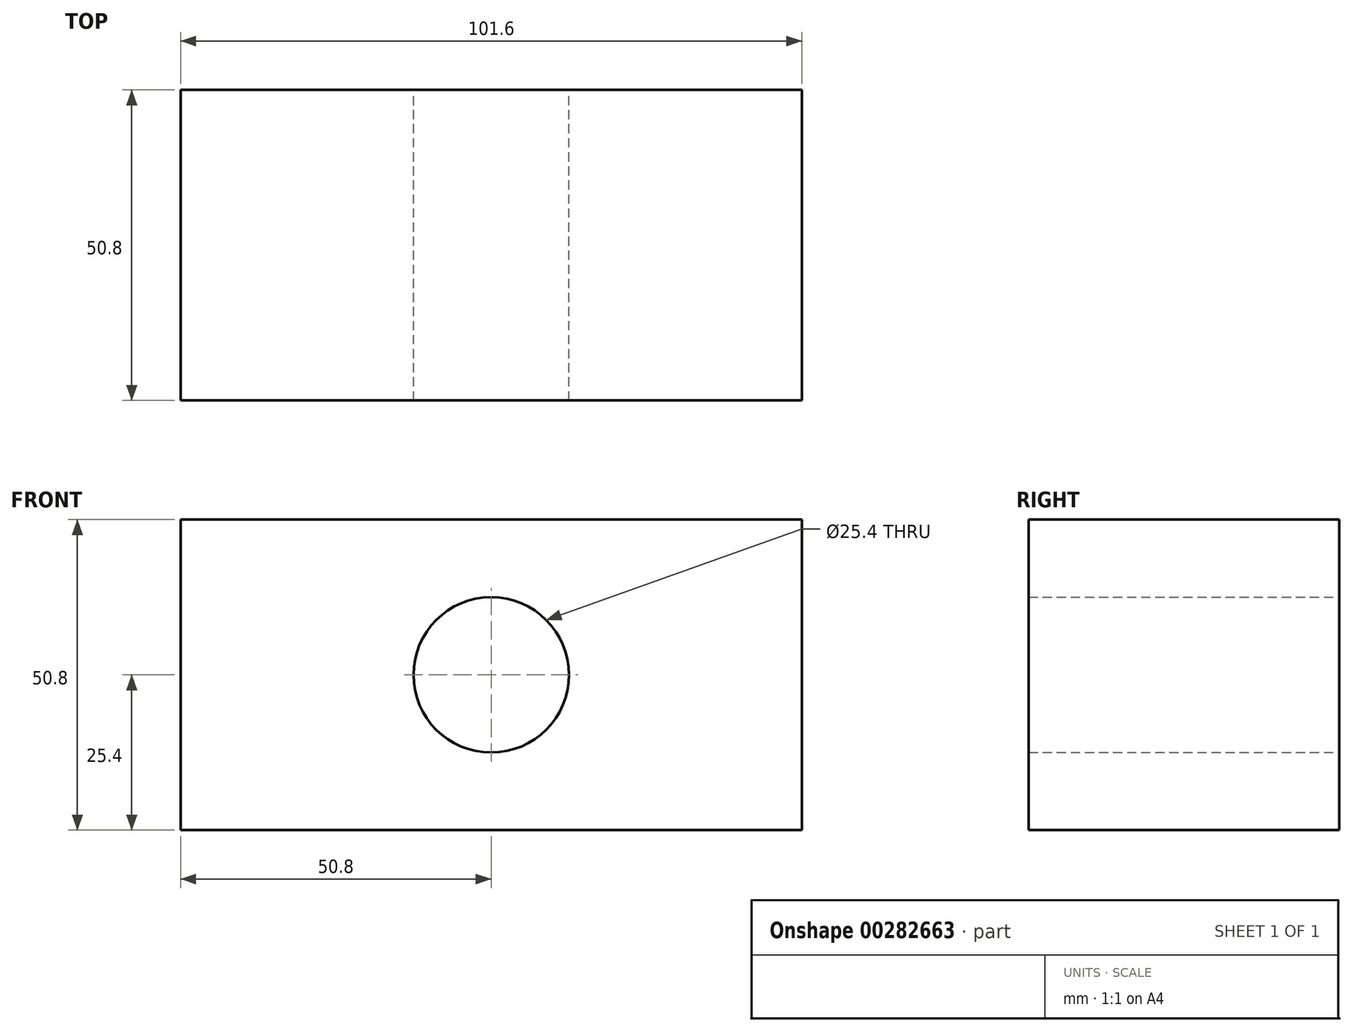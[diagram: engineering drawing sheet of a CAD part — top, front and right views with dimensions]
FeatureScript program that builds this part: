
annotation { "Feature Type Name" : "Feature", "Feature Type Description" : "" }
export const myFeature = defineFeature(function(context is Context, id is Id, definition is map)
    precondition{}
    {
        {
            var Q0;
            Q0=qCreatedBy(makeId("Front.planeOp"),FACE);
            var sketch = newSketch(context, id + "F0", { "sketchPlane" : qUnion([Q0])});
            skLineSegment(sketch, "E0.bottom", {"start": v(50.8, -25.4) * mm, "end": v(-50.8, -25.4) * mm});
            skLineSegment(sketch, "E0.top", {"start": v(50.8, 25.4) * mm, "end": v(-50.8, 25.4) * mm});
            skLineSegment(sketch, "E0.left", {"start": v(50.8, -25.4) * mm, "end": v(50.8, 25.4) * mm});
            skLineSegment(sketch, "E0.right", {"start": v(-50.8, -25.4) * mm, "end": v(-50.8, 25.4) * mm});
            skPoint(sketch, "E0.middle", {"position": v(0, 0) * mm});
            skCircle(sketch, "E1", {"center": v(0, 0) * mm, "radius": 12.7 * mm});
            skSolve(sketch);
        }
        {
            var Q0;
            Q0 = qSketchRegion(id + "F0", true);
            extrude(context, id + "F1", {"entities" : qUnion([Q0]), "depth" : 50.8 * mm});
        }
    });
